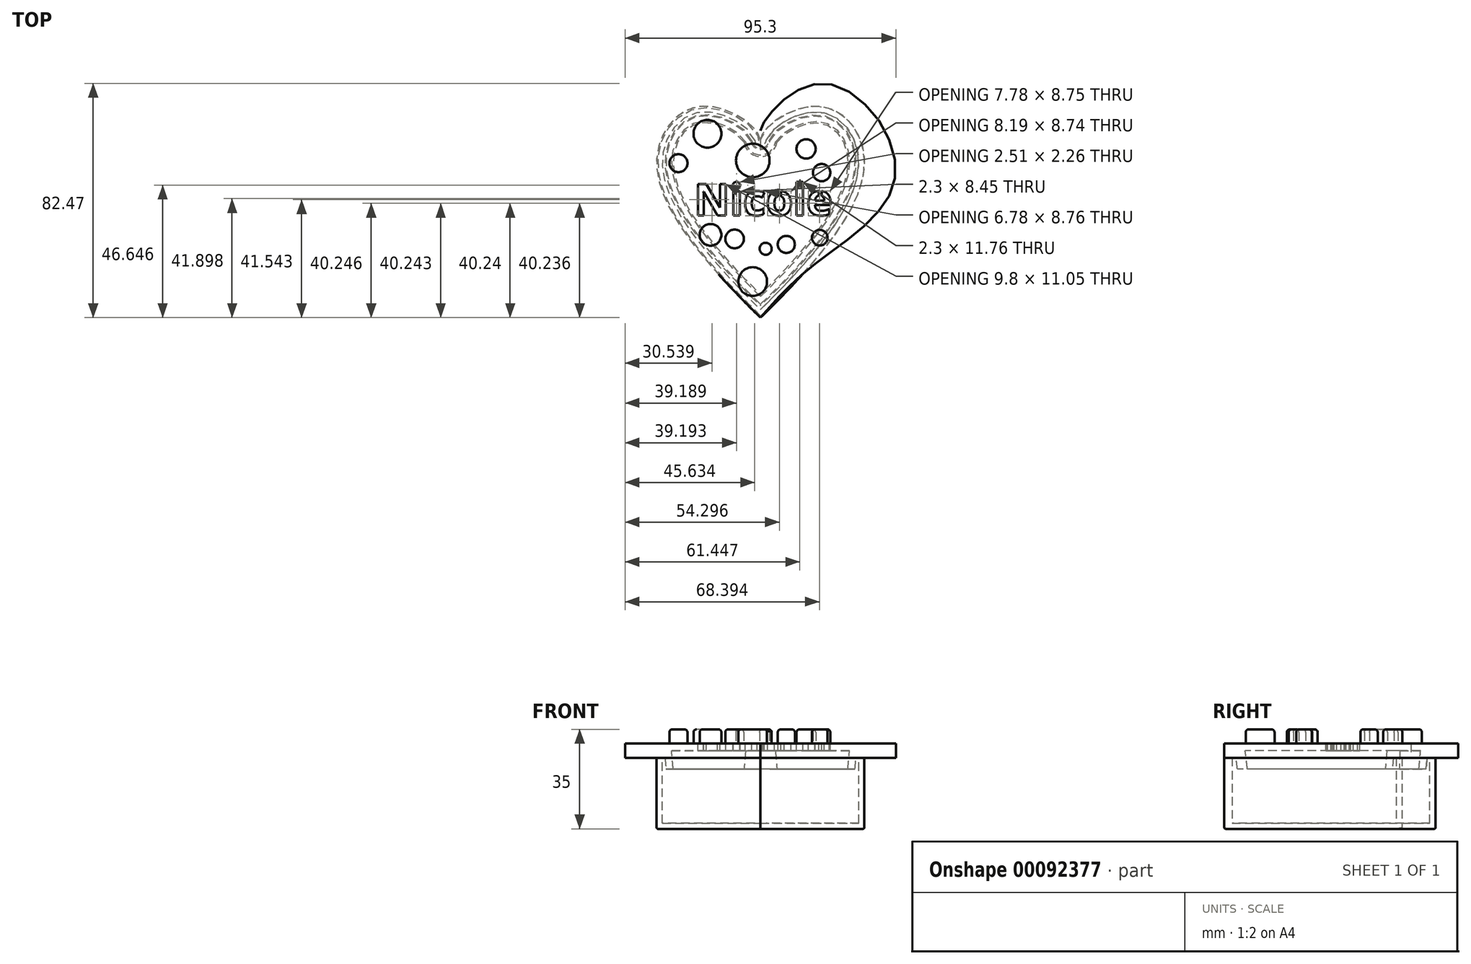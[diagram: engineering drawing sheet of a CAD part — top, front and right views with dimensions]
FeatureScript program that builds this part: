
annotation { "Feature Type Name" : "Feature", "Feature Type Description" : "" }
export const myFeature = defineFeature(function(context is Context, id is Id, definition is map)
    precondition{}
    {
        {
            var Q0;
            Q0=qCreatedBy(makeId("Top.planeOp"),FACE);
            var sketch = newSketch(context, id + "F0", { "sketchPlane" : qUnion([Q0])});
            skFitSpline(sketch, "E0", {"points": [v(0, 62.61) * mm, v(-20.45, 74.43) * mm, v(-36.6, 54.89) * mm, v(0, 0) * mm], "startDerivative": vector(-8.04, 57.41) * mm, "endDerivative": vector(128.56, -126.3) * mm});
            skLineSegment(sketch, "E1", {"start": v(0, 52.07) * mm, "end": v(0, -53.92) * mm, "construction": true});
            skFitSpline(sketch, "E2.MirrorCS", {"points": [v(0, 62.61) * mm, v(20.45, 74.43) * mm, v(36.6, 54.89) * mm, v(0, 0) * mm], "startDerivative": vector(8.04, 57.41) * mm, "endDerivative": vector(-128.56, -126.3) * mm});
            skSolve(sketch);
        }
        {
            var Q0;
            Q0 = qSketchRegion(id + "F0", true);
            extrude(context, id + "F1", {"entities" : qUnion([Q0]), "depth" : 25 * mm});
        }
        {
            var Q0;
            Q0=makeQuery(id+"F1.opExtrude","CAP_EDGE",EDGE,{"disambiguationData":[OSD([sQuery(id+"F0.wireOp",EDGE,"E0")])],"isStart":true});
            var Q1;
            Q1=makeQuery(id+"F1.opExtrude","CAP_EDGE",EDGE,{"disambiguationData":[OSD([sQuery(id+"F0.wireOp",EDGE,"E2.MirrorCS")])],"isStart":true});
            fillet(context, id + "F2", {"entities" : qUnion([Q0, Q1]), "radius" : 0.5 * mm, "tangentPropagation" : true, "allowEdgeOverflow" : false});
        }
        {
            var Q0;
            Q0=makeQuery(id+"F1.opExtrude","CAP_FACE",FACE,{"disambiguationData":[OSD([sQuery(id+"F0.wireOp",EDGE,"E0"),sQuery(id+"F0.wireOp",EDGE,"E2.MirrorCS")])],"isStart":false});
            shell(context, id + "F3", {"entities" : qUnion([Q0]), "thickness" : 2 * mm});
        }
        {
            var Q0;
            {var subQ0=sQuery(id+"F0.wireOp",EDGE,"E2.MirrorCS");var subQ1=sQuery(id+"F0.wireOp",EDGE,"E0");Q0=makeQuery(id+"F3.opShell","OFFSET_EDGE",EDGE,{"disambiguationData":[OSD([subQ1,subQ0]),TDD([makeQuery(id+"F1.opExtrude","SWEPT_EDGE",EDGE,{"disambiguationData":[OSD([subQ1,subQ0]),TDD([makeQuery(id+"F0.imprint","INTERSECT",VERTEX,{"disambiguationData":[OD(0.0)],"derivedFrom":[subQ1,subQ0]})])]})])]});}
            fillet(context, id + "F4", {"entities" : qUnion([Q0]), "radius" : 2 * mm, "tangentPropagation" : true, "allowEdgeOverflow" : false});
        }
        {
            var Q0;
            Q0=makeQuery(id+"F1.opExtrude","CAP_FACE",FACE,{"disambiguationData":[OSD([sQuery(id+"F0.wireOp",EDGE,"E0"),sQuery(id+"F0.wireOp",EDGE,"E2.MirrorCS")])],"isStart":false});
            var sketch = newSketch(context, id + "F5", { "sketchPlane" : qUnion([Q0])});
            skFitSpline(sketch, "E3.0", {"points": [v(0, 62.61) * mm, v(-0.72, 67.78) * mm, v(-22.94, 82.43) * mm, v(-47.6, 50.7) * mm, v(-19.32, 18.98) * mm, v(0, 0) * mm]});
            skFitSpline(sketch, "E4.0", {"points": [v(0, 62.61) * mm, v(0.72, 67.78) * mm, v(22.94, 82.43) * mm, v(47.6, 50.7) * mm, v(19.32, 18.98) * mm, v(0, 0) * mm]});
            skSolve(sketch);
        }
        {
            var Q0;
            Q0 = qSketchRegion(id + "F5", true);
            extrude(context, id + "F6", {"entities" : qUnion([Q0]), "depth" : 5 * mm});
        }
        {
            var Q0;
            Q0=makeQuery(id+"F6.opExtrude","CAP_FACE",FACE,{"disambiguationData":[OSD([sQuery(id+"F5.wireOp",EDGE,"E3.0"),sQuery(id+"F5.wireOp",EDGE,"E4.0")])],"isStart":true});
            var sketch = newSketch(context, id + "F7", { "sketchPlane" : qUnion([Q0])});
            skFitSpline(sketch, "E5.0", {"points": [v(2.97, -62.2) * mm, v(2.98, -62.28) * mm, v(3.03, -62.52) * mm, v(3.26, -63.05) * mm, v(3.67, -63.7) * mm, v(4.43, -64.7) * mm, v(5.8, -66.04) * mm, v(7.93, -67.65) * mm, v(10.44, -69.1) * mm, v(13.17, -70.29) * mm, v(15.5, -70.98) * mm, v(17.34, -71.32) * mm, v(18.67, -71.46) * mm, v(19.95, -71.47) * mm, v(21.57, -71.33) * mm, v(23.5, -70.86) * mm, v(25.67, -69.85) * mm, v(28.33, -67.95) * mm, v(30.57, -65.28) * mm, v(32.2, -62.04) * mm, v(33.08, -59.38) * mm, v(33.49, -57.02) * mm, v(33.6, -55.08) * mm, v(33.58, -53.1) * mm, v(33.27, -50.53) * mm, v(32.46, -47.3) * mm, v(31.24, -43.92) * mm, v(29.08, -39.27) * mm, v(25.45, -33.2) * mm, v(19.83, -25.62) * mm, v(10.99, -15.28) * mm, v(3.23, -7.38) * mm, v(-2.1, -2.14) * mm]});
            skFitSpline(sketch, "E6.0", {"points": [v(-2.97, -62.2) * mm, v(-2.98, -62.28) * mm, v(-3.03, -62.52) * mm, v(-3.26, -63.05) * mm, v(-3.67, -63.7) * mm, v(-4.43, -64.7) * mm, v(-5.8, -66.04) * mm, v(-7.93, -67.65) * mm, v(-10.44, -69.1) * mm, v(-13.17, -70.29) * mm, v(-15.5, -70.98) * mm, v(-17.34, -71.32) * mm, v(-18.67, -71.46) * mm, v(-19.95, -71.47) * mm, v(-21.57, -71.33) * mm, v(-23.5, -70.86) * mm, v(-25.67, -69.85) * mm, v(-28.33, -67.95) * mm, v(-30.57, -65.28) * mm, v(-32.2, -62.04) * mm, v(-33.08, -59.38) * mm, v(-33.49, -57.02) * mm, v(-33.6, -55.08) * mm, v(-33.58, -53.1) * mm, v(-33.27, -50.53) * mm, v(-32.46, -47.3) * mm, v(-31.24, -43.92) * mm, v(-29.08, -39.27) * mm, v(-25.45, -33.2) * mm, v(-19.83, -25.62) * mm, v(-10.99, -15.28) * mm, v(-3.23, -7.38) * mm, v(2.1, -2.14) * mm]});
            skArc(sketch, "E7", {"start": v(2.97, -62.2) * mm, "mid": v(0, -59.61) * mm, "end": v(-2.97, -62.2) * mm});
            skSolve(sketch);
        }
        {
            var Q0;
            Q0 = qSketchRegion(id + "F7", true);
            extrude(context, id + "F8", {"entities" : qUnion([Q0]), "operationType" : NewBodyOperationType.ADD, "depth" : 4 * mm, "hasDraft" : true, "draftAngle" : 5 * degree, "draftPullDirection" : true});
        }
        {
            var Q0;
            Q0=makeQuery(id+"F8.opExtrude","CAP_FACE",FACE,{"disambiguationData":[OSD([sQuery(id+"F7.wireOp",EDGE,"E5.0"),sQuery(id+"F7.wireOp",EDGE,"E6.0"),sQuery(id+"F7.wireOp",EDGE,"E7")])],"isStart":false});
            shell(context, id + "F9", {"entities" : qUnion([Q0]), "thickness" : 2.5 * mm});
        }
        {
            var Q0;
            Q0=makeQuery(id+"F6.opExtrude","CAP_FACE",FACE,{"disambiguationData":[OSD([sQuery(id+"F5.wireOp",EDGE,"E3.0"),sQuery(id+"F5.wireOp",EDGE,"E4.0")])],"isStart":false});
            var sketch = newSketch(context, id + "F10", { "sketchPlane" : qUnion([Q0])});
            skText(sketch, "E8", { "text": "Nicole", "fontName": "OpenSans-Bold.ttf"});
            const initialGuessF10  = {"E8": [-0.0234, 0.03602, 1, 0, 0.01114]};
            skSetInitialGuess(sketch, initialGuessF10);
            skSolve(sketch);
        }
        {
            var Q0;
            Q0 = qSketchRegion(id + "F10", true);
            extrude(context, id + "F11", {"entities" : qUnion([Q0]), "operationType" : NewBodyOperationType.REMOVE, "oppositeDirection" : true, "depth" : 25 * mm});
        }
        {
            var Q0;
            Q0=makeQuery(id+"F11.boolean.opBoolean","SPLIT",FACE,{"disambiguationData":[TD([makeQuery(id+"F11.opExtrude","SWEPT_FACE",FACE,{"disambiguationData":[OSD([sQuery(id+"F10.wireOp",EDGE,"E8.sketch_text.stroke-37")])]})])],"derivedFrom":makeQuery(id+"F6.opExtrude","CAP_FACE",FACE,{"disambiguationData":[OSD([sQuery(id+"F5.wireOp",EDGE,"E3.0"),sQuery(id+"F5.wireOp",EDGE,"E4.0")])],"isStart":false})});
            var sketch = newSketch(context, id + "F12", { "sketchPlane" : qUnion([Q0])});
            skLineSegment(sketch, "E9.bottom", {"start": v(6.18, 42.14) * mm, "end": v(7.2, 42.14) * mm});
            skLineSegment(sketch, "E9.top", {"start": v(6.18, 45.9) * mm, "end": v(7.2, 45.9) * mm});
            skLineSegment(sketch, "E9.left", {"start": v(6.18, 42.14) * mm, "end": v(6.18, 45.9) * mm});
            skLineSegment(sketch, "E9.right", {"start": v(7.2, 42.14) * mm, "end": v(7.2, 45.9) * mm});
            skLineSegment(sketch, "E10.bottom", {"start": v(20.5, 42.4) * mm, "end": v(21.54, 42.4) * mm});
            skLineSegment(sketch, "E10.top", {"start": v(20.5, 46.54) * mm, "end": v(21.54, 46.54) * mm});
            skLineSegment(sketch, "E10.left", {"start": v(20.5, 42.4) * mm, "end": v(20.5, 46.54) * mm});
            skLineSegment(sketch, "E10.right", {"start": v(21.54, 42.4) * mm, "end": v(21.54, 46.54) * mm});
            skSolve(sketch);
        }
        {
            var Q0;
            Q0 = qSketchRegion(id + "F12", true);
            var Q1;
            Q1=makeQuery(id+"F1.opExtrude","SWEPT_FACE",FACE,{"disambiguationData":[OSD([sQuery(id+"F0.wireOp",EDGE,"E2.MirrorCS")])]});
            extrude(context, id + "F13", {"entities" : qUnion([Q0]), "operationType" : NewBodyOperationType.ADD, "oppositeDirection" : true, "endBoundEntityFace" : qUnion([Q1]), "depth" : 2.5 * mm});
        }
        {
            var Q0;
            {var subQ0=sQuery(id+"F5.wireOp",EDGE,"E3.0");var subQ1=sQuery(id+"F5.wireOp",EDGE,"E4.0");var subQ2=makeQuery(id+"F6.opExtrude","CAP_FACE",FACE,{"disambiguationData":[OSD([subQ0,subQ1])],"isStart":false});Q0=makeQuery(id+"F13.boolean.opBoolean","MERGE",FACE,{"derivedFrom":[makeQuery(id+"F11.boolean.opBoolean","SPLIT",FACE,{"disambiguationData":[TD([makeQuery(id+"F11.opExtrude","SWEPT_FACE",FACE,{"disambiguationData":[OSD([sQuery(id+"F10.wireOp",EDGE,"E8.sketch_text.stroke-37")])]})])],"derivedFrom":subQ2}),makeQuery(id+"F11.boolean.opBoolean","SPLIT",FACE,{"disambiguationData":[TD([makeQuery(id+"F11.opExtrude","SWEPT_FACE",FACE,{"disambiguationData":[OSD([sQuery(id+"F10.wireOp",EDGE,"E8.sketch_text.stroke-59")])]})])],"derivedFrom":subQ2}),makeQuery(id+"F11.boolean.opBoolean","SPLIT",FACE,{"disambiguationData":[TD([makeQuery(id+"F6.opExtrude","SWEPT_FACE",FACE,{"disambiguationData":[OSD([subQ0])]})])],"derivedFrom":subQ2}),makeQuery(id+"F13.opExtrude","CAP_FACE",FACE,{"disambiguationData":[OSD([sQuery(id+"F12.wireOp",EDGE,"E9.bottom"),sQuery(id+"F12.wireOp",EDGE,"E9.top"),sQuery(id+"F12.wireOp",EDGE,"E9.left"),sQuery(id+"F12.wireOp",EDGE,"E9.right")])],"isStart":true}),makeQuery(id+"F13.opExtrude","CAP_FACE",FACE,{"disambiguationData":[OSD([sQuery(id+"F12.wireOp",EDGE,"E10.bottom"),sQuery(id+"F12.wireOp",EDGE,"E10.top"),sQuery(id+"F12.wireOp",EDGE,"E10.left"),sQuery(id+"F12.wireOp",EDGE,"E10.right")])],"isStart":true})]});}
            var sketch = newSketch(context, id + "F14", { "sketchPlane" : qUnion([Q0])});
            skCircle(sketch, "E11", {"center": v(-28.9, 54.4) * mm, "radius": 3.16 * mm});
            skCircle(sketch, "E12", {"center": v(16.08, 59.4) * mm, "radius": 3.38 * mm});
            skCircle(sketch, "E13", {"center": v(-9.13, 27.71) * mm, "radius": 3.27 * mm});
            skCircle(sketch, "E14", {"center": v(1.82, 24.25) * mm, "radius": 2.13 * mm});
            skCircle(sketch, "E15", {"center": v(9.09, 25.79) * mm, "radius": 3.01 * mm});
            skCircle(sketch, "E16", {"center": v(-18.68, 64.75) * mm, "radius": 4.9 * mm});
            skCircle(sketch, "E17", {"center": v(21.54, 51.05) * mm, "radius": 3.04 * mm});
            skCircle(sketch, "E18", {"center": v(-2.76, 12.7) * mm, "radius": 5.06 * mm});
            skCircle(sketch, "E19", {"center": v(-2.7, 55.34) * mm, "radius": 5.9 * mm});
            skCircle(sketch, "E20", {"center": v(20.87, 28.15) * mm, "radius": 2.75 * mm});
            skCircle(sketch, "E21", {"center": v(-17.6, 29.16) * mm, "radius": 3.82 * mm});
            skSolve(sketch);
        }
        {
            var Q0;
            Q0 = qSketchRegion(id + "F14", true);
            extrude(context, id + "F15", {"entities" : qUnion([Q0]), "operationType" : NewBodyOperationType.ADD, "depth" : 5 * mm});
        }
        {
            var Q0;
            Q0=makeQuery(id+"F15.opExtrude","CAP_FACE",FACE,{"disambiguationData":[OSD([sQuery(id+"F14.wireOp",EDGE,"E16")])],"isStart":false});
            var Q1;
            Q1=makeQuery(id+"F15.opExtrude","CAP_EDGE",EDGE,{"disambiguationData":[OSD([sQuery(id+"F14.wireOp",EDGE,"E11")])],"isStart":false});
            fillet(context, id + "F16", {"entities" : qUnion([Q0, Q1]), "radius" : 1 * mm, "tangentPropagation" : true, "allowEdgeOverflow" : false});
        }
        {
            var Q0;
            Q0=makeQuery(id+"F15.opExtrude","CAP_EDGE",EDGE,{"disambiguationData":[OSD([sQuery(id+"F14.wireOp",EDGE,"E21")])],"isStart":false});
            var Q1;
            Q1=makeQuery(id+"F15.opExtrude","CAP_FACE",FACE,{"disambiguationData":[OSD([sQuery(id+"F14.wireOp",EDGE,"E18")])],"isStart":false});
            var Q2;
            Q2=makeQuery(id+"F15.opExtrude","CAP_EDGE",EDGE,{"disambiguationData":[OSD([sQuery(id+"F14.wireOp",EDGE,"E13")])],"isStart":false});
            var Q3;
            Q3=makeQuery(id+"F15.opExtrude","CAP_EDGE",EDGE,{"disambiguationData":[OSD([sQuery(id+"F14.wireOp",EDGE,"E14")])],"isStart":false});
            var Q4;
            Q4=makeQuery(id+"F15.opExtrude","CAP_EDGE",EDGE,{"disambiguationData":[OSD([sQuery(id+"F14.wireOp",EDGE,"E15")])],"isStart":false});
            var Q5;
            Q5=makeQuery(id+"F15.opExtrude","CAP_FACE",FACE,{"disambiguationData":[OSD([sQuery(id+"F14.wireOp",EDGE,"E20")])],"isStart":false});
            var Q6;
            Q6=makeQuery(id+"F15.opExtrude","CAP_FACE",FACE,{"disambiguationData":[OSD([sQuery(id+"F14.wireOp",EDGE,"E17")])],"isStart":false});
            var Q7;
            Q7=makeQuery(id+"F15.opExtrude","CAP_FACE",FACE,{"disambiguationData":[OSD([sQuery(id+"F14.wireOp",EDGE,"E12")])],"isStart":false});
            var Q8;
            Q8=makeQuery(id+"F15.opExtrude","CAP_EDGE",EDGE,{"disambiguationData":[OSD([sQuery(id+"F14.wireOp",EDGE,"E19")])],"isStart":false});
            fillet(context, id + "F17", {"entities" : qUnion([Q0, Q1, Q2, Q3, Q4, Q5, Q6, Q7, Q8]), "radius" : 1 * mm, "tangentPropagation" : true, "allowEdgeOverflow" : false});
        }
    });
